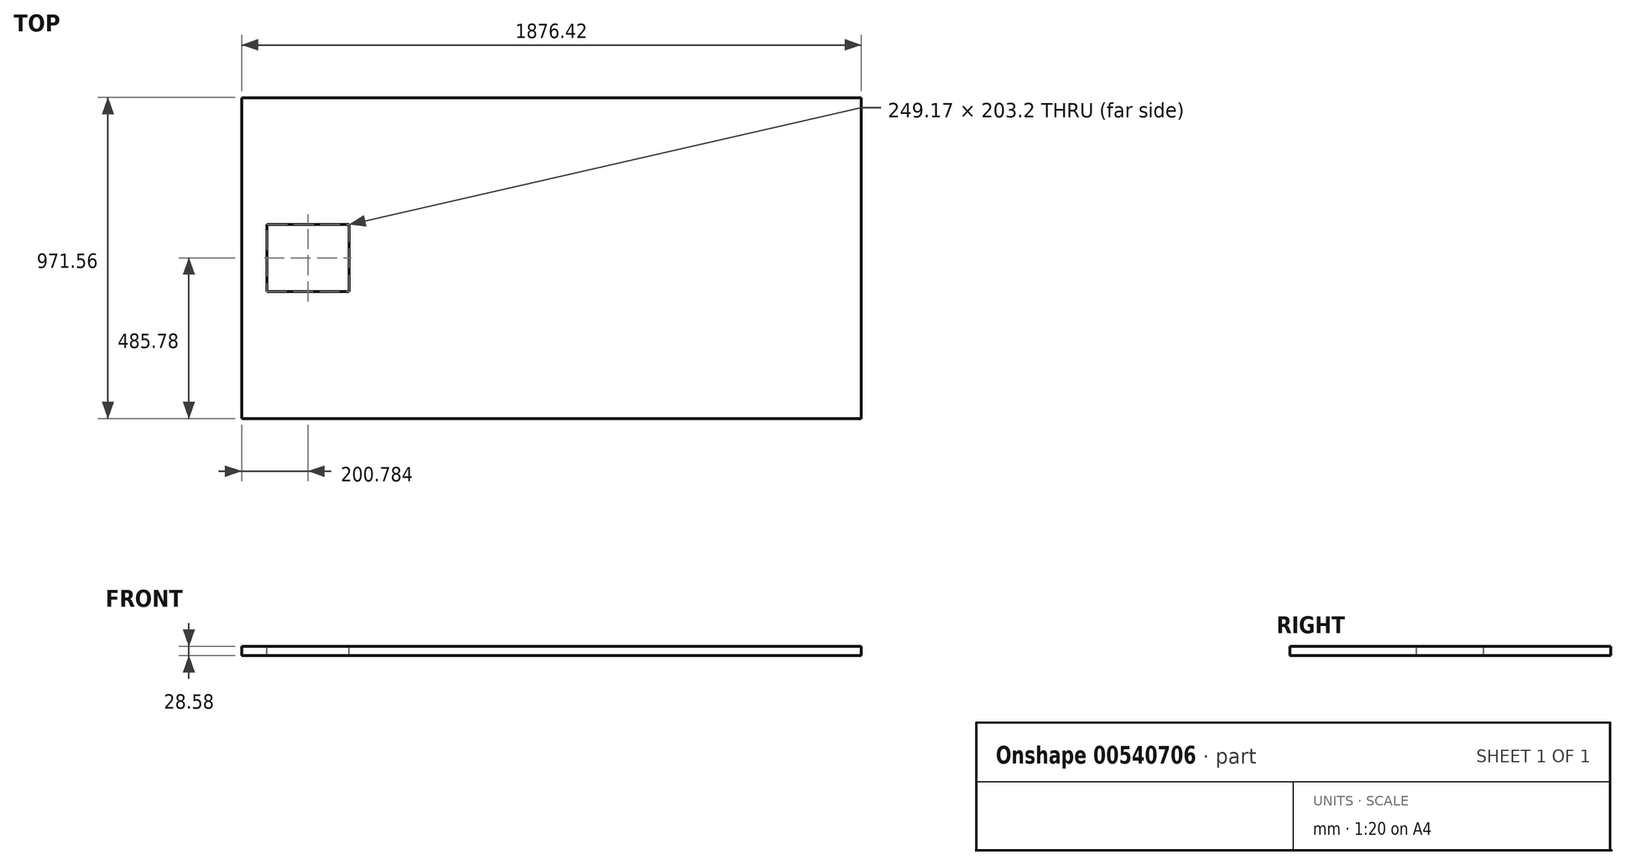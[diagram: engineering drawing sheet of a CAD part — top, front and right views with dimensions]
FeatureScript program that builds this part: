
annotation { "Feature Type Name" : "Feature", "Feature Type Description" : "" }
export const myFeature = defineFeature(function(context is Context, id is Id, definition is map)
    precondition{}
    {
        {
            var Q0;
            Q0=qCreatedBy(makeId("Top.planeOp"),FACE);
            var sketch = newSketch(context, id + "F0", { "sketchPlane" : qUnion([Q0])});
            skLineSegment(sketch, "E0.bottom", {"start": v(938.21, 485.78) * mm, "end": v(-938.21, 485.77) * mm});
            skLineSegment(sketch, "E0.top", {"start": v(938.21, -485.77) * mm, "end": v(-938.21, -485.78) * mm});
            skLineSegment(sketch, "E0.left", {"start": v(938.21, 485.78) * mm, "end": v(938.21, -485.77) * mm});
            skLineSegment(sketch, "E0.right", {"start": v(-938.21, 485.77) * mm, "end": v(-938.21, -485.78) * mm});
            skPoint(sketch, "E0.middle", {"position": v(0, 0) * mm});
            skSolve(sketch);
        }
        {
            var Q0;
            Q0=makeQuery(id+"F0.imprint","IMPRINT",FACE,{"disambiguationData":[TD([[makeQuery(id+"F0.imprint","IMPRINT",EDGE,{"derivedFrom":sQuery(id+"F0.wireOp",EDGE,"E0.bottom")}),1.0]])]});
            extrude(context, id + "F1", {"entities" : qUnion([Q0]), "depth" : 28.57 * mm, "offsetDistance" : 25.4 * mm});
        }
        {
            var Q0;
            Q0=makeQuery(id+"F1.opExtrude","CAP_FACE",FACE,{"disambiguationData":[OSD([sQuery(id+"F0.wireOp",EDGE,"E0.bottom"),sQuery(id+"F0.wireOp",EDGE,"E0.top"),sQuery(id+"F0.wireOp",EDGE,"E0.left"),sQuery(id+"F0.wireOp",EDGE,"E0.right")])],"isStart":false});
            var sketch = newSketch(context, id + "F2", { "sketchPlane" : qUnion([Q0])});
            skLineSegment(sketch, "E1", {"start": v(-938.21, 0) * mm, "end": v(-737.43, 0) * mm});
            skPoint(sketch, "E1.endSnap0", {"position": v(-938.21, 0) * mm});
            skLineSegment(sketch, "E2.bottom", {"start": v(-612.84, 101.6) * mm, "end": v(-862.01, 101.6) * mm});
            skLineSegment(sketch, "E2.top", {"start": v(-612.84, -101.6) * mm, "end": v(-862.01, -101.6) * mm});
            skLineSegment(sketch, "E2.left", {"start": v(-612.84, 101.6) * mm, "end": v(-612.84, -101.6) * mm});
            skLineSegment(sketch, "E2.right", {"start": v(-862.01, 101.6) * mm, "end": v(-862.01, -101.6) * mm});
            skPoint(sketch, "E2.middle", {"position": v(-737.43, 0) * mm});
            skSolve(sketch);
        }
        {
            var Q0;
            {var subQ1=sQuery(id+"F2.wireOp",EDGE,"E2.bottom");Q0=makeQuery(id+"F2.imprint","IMPRINT",FACE,{"disambiguationData":[TD([[makeQuery(id+"F2.imprint","IMPRINT",EDGE,{"derivedFrom":subQ1}),1.0]])]});}
            extrude(context, id + "F3", {"entities" : qUnion([Q0]), "operationType" : NewBodyOperationType.REMOVE, "oppositeDirection" : true, "depth" : 38.1 * mm, "offsetDistance" : 25.4 * mm});
        }
    });
